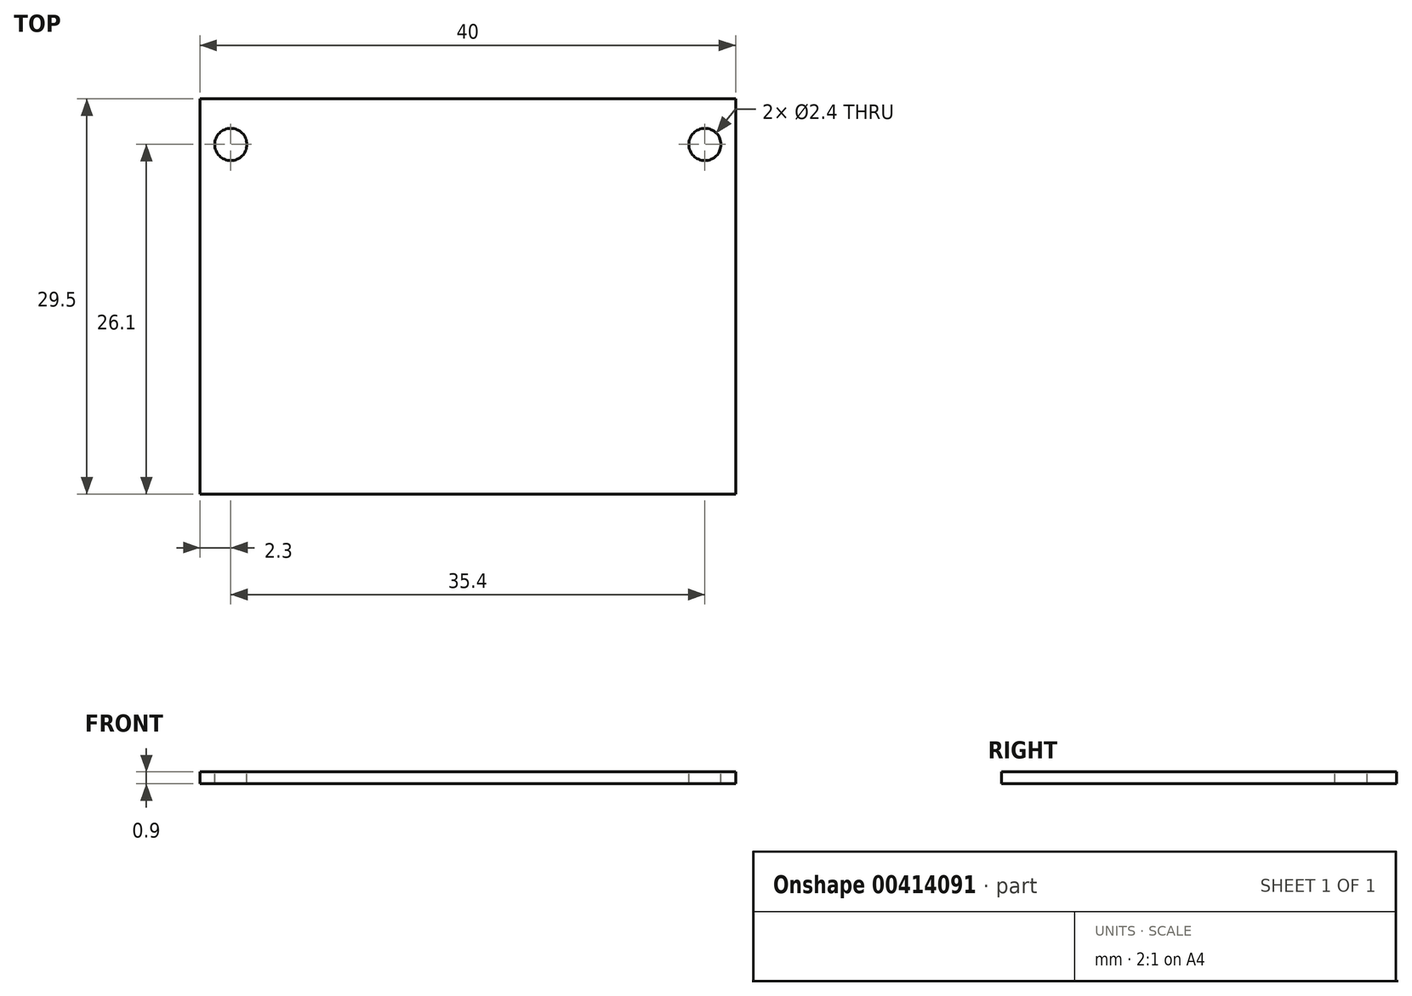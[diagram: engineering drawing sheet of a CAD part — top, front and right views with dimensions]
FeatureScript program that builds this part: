
annotation { "Feature Type Name" : "Feature", "Feature Type Description" : "" }
export const myFeature = defineFeature(function(context is Context, id is Id, definition is map)
    precondition{}
    {
        {
            var Q0;
            Q0=qCreatedBy(makeId("Top.planeOp"),FACE);
            var sketch = newSketch(context, id + "F0", { "sketchPlane" : qUnion([Q0])});
            skLineSegment(sketch, "E0.bottom", {"start": v(0, 0) * mm, "end": v(40, 0) * mm});
            skLineSegment(sketch, "E0.top", {"start": v(0, 29.5) * mm, "end": v(40, 29.5) * mm});
            skLineSegment(sketch, "E0.left", {"start": v(0, 0) * mm, "end": v(0, 29.5) * mm});
            skLineSegment(sketch, "E0.right", {"start": v(40, 0) * mm, "end": v(40, 29.5) * mm});
            skSolve(sketch);
        }
        {
            var Q0;
            Q0=makeQuery(id+"F0.imprint","IMPRINT",FACE,{"disambiguationData":[TD([[makeQuery(id+"F0.imprint","IMPRINT",EDGE,{"derivedFrom":sQuery(id+"F0.wireOp",EDGE,"E0.bottom")}),1.0]])]});
            extrude(context, id + "F1", {"entities" : qUnion([Q0]), "depth" : .9 * mm});
        }
        {
            var Q0;
            Q0=makeQuery(id+"F1.opExtrude","CAP_FACE",FACE,{"disambiguationData":[OSD([sQuery(id+"F0.wireOp",EDGE,"E0.bottom"),sQuery(id+"F0.wireOp",EDGE,"E0.top"),sQuery(id+"F0.wireOp",EDGE,"E0.left"),sQuery(id+"F0.wireOp",EDGE,"E0.right")])],"isStart":false});
            var sketch = newSketch(context, id + "F2", { "sketchPlane" : qUnion([Q0])});
            skLineSegment(sketch, "E1.bottom", {"start": v(0, 29.5) * mm, "end": v(1.1, 29.5) * mm});
            skLineSegment(sketch, "E1.left", {"start": v(0, 29.5) * mm, "end": v(0, 27.3) * mm});
            skCircle(sketch, "E2", {"center": v(2.3, 26.1) * mm, "radius": 1.2 * mm});
            skLineSegment(sketch, "E3.bottom", {"start": v(40, 29.5) * mm, "end": v(38.9, 29.5) * mm});
            skLineSegment(sketch, "E3.left", {"start": v(40, 29.5) * mm, "end": v(40, 27.3) * mm});
            skCircle(sketch, "E4", {"center": v(37.7, 26.1) * mm, "radius": 1.2 * mm});
            skPoint(sketch, "E5.orphan", {"position": v(1.1, 27.3) * mm});
            skPoint(sketch, "E6.orphan", {"position": v(1.1, 24.9) * mm});
            skPoint(sketch, "E7.bottom.start.orphan", {"position": v(2.3, 27.3) * mm});
            skPoint(sketch, "E8.orphan", {"position": v(3.5, 27.3) * mm});
            skPoint(sketch, "E7.top.end.orphan", {"position": v(3.5, 24.9) * mm});
            skPoint(sketch, "E7.top.start.orphan", {"position": v(2.3, 24.9) * mm});
            skPoint(sketch, "E9.orphan", {"position": v(38.9, 27.3) * mm});
            skPoint(sketch, "E10.bottom.end.orphan", {"position": v(36.5, 27.3) * mm});
            skPoint(sketch, "E11.orphan", {"position": v(36.5, 24.9) * mm});
            skPoint(sketch, "E10.left.end.orphan", {"position": v(38.9, 24.9) * mm});
            skPoint(sketch, "E12.orphan", {"position": v(37.7, 24.9) * mm});
            skPoint(sketch, "E13.start.orphan", {"position": v(37.7, 27.3) * mm});
            skSolve(sketch);
        }
        {
            var Q0;
            Q0=makeQuery(id+"F2.imprint","IMPRINT",FACE,{"disambiguationData":[TD([[makeQuery(id+"F2.imprint","IMPRINT",EDGE,{"derivedFrom":sQuery(id+"F2.wireOp",EDGE,"E2")}),1.0]])]});
            var Q1;
            Q1=makeQuery(id+"F2.imprint","IMPRINT",FACE,{"disambiguationData":[TD([[makeQuery(id+"F2.imprint","IMPRINT",EDGE,{"derivedFrom":sQuery(id+"F2.wireOp",EDGE,"E4")}),1.0]])]});
            extrude(context, id + "F3", {"entities" : qUnion([Q0, Q1]), "operationType" : NewBodyOperationType.REMOVE, "oppositeDirection" : true, "depth" : 25.4 * mm});
        }
    });
